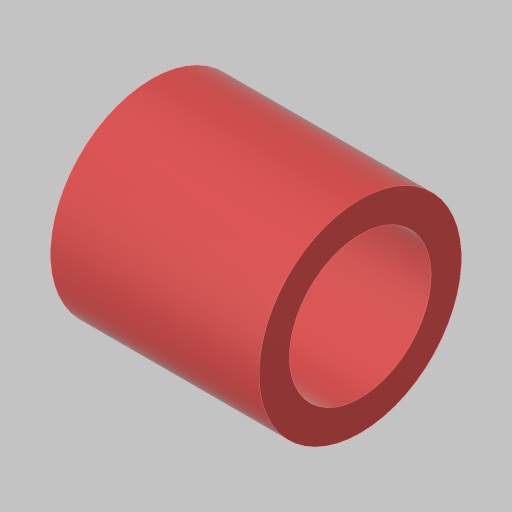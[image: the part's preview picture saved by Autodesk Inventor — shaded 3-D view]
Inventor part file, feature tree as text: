
AUTODESK INVENTOR PART (.ipt)
format: ipt  version: 2023.5 (Build 275446000, 446)  size: 118,272 bytes
history: native  units: in
note: dims shown in document units (in); Inventor stores cm internally (conversion verified against a paired STEP export)
features: extrude x1, sketch x1
ambient origin geometry x8: Origin, YZ Plane, XZ Plane, XY Plane, X Axis, Y Axis, Z Axis, Center Point
bodies: Solid1 (feature_tree)
feature tree (2):
  extrude  "Extrusion1"  Depth=0.86in
  sketch  "Sketch1"  dims[d0=0.585in d1=0.125in d2=0.86in d3=0.0in]
